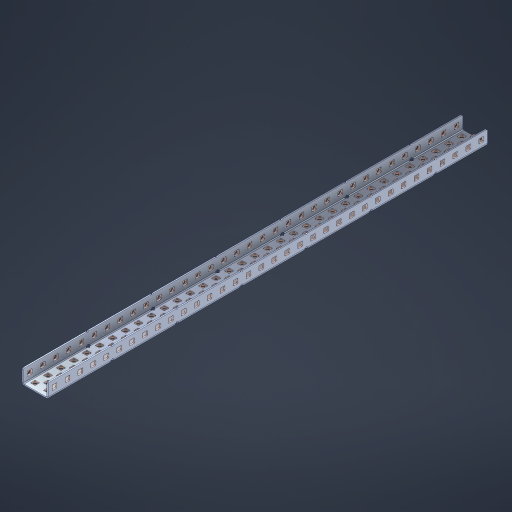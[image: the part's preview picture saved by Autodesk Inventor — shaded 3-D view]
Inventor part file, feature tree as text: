
AUTODESK INVENTOR PART (.ipt)
format: ipt  version: 2023 (Build 270158000, 158)  size: 2,078,720 bytes
history: native  units: in
note: dims shown in document units (in); Inventor stores cm internally (conversion verified against a paired STEP export)
features: other x177, extrude x168, sheet_metal_op x11, sketch x10, pattern_linear x2, mirror x1, chamfer x1
ambient origin geometry x8: Origin, YZ Plane, XZ Plane, XY Plane, X Axis, Y Axis, Z Axis, Center Point
bodies: Solid1 (feature_tree), Body (feature_tree)
feature tree (370):
  sheet_metal_op  "Flanges"
  other  "Flange Pattern Plane"
  other  "Flange Pattern Sketch"
  sheet_metal_op  "Flange Pattern"
  sheet_metal_op  "Body Pattern"
  pattern_linear  "Center Pattern"  Spacing1=0.0469in  [1 undecoded]
  other  "Arc Length"
  mirror  "Notch Mirror"
  pattern_linear  "Notch Pattern"  Spacing1=0.182in  [1 undecoded]
  chamfer  "End Chamfer"
  extrude  "Half Cut"  Depth=0.02in
  sketch  "Sketch1"  dims[d0=1.0in]
  other  "Plate1"
  sketch  "Sketch2"  dims[d1=17.0in]
  other  "Plate2"
  sheet_metal_op  "Bend1"
  sheet_metal_op  "Corner1"
  sketch  "Sketch3"  dims[d2=0.0469in]
  sketch  "Sketch7"  dims[d3=0.0469in]
  other  "Srf1"
  other  "Srf2"
  sketch  "Sketch8"  dims[d4=0.0234in]
  sketch  "Sketch9"  dims[d5=0.0938in]
  other  "Srf91"
  sheet_metal_op  "Body Pattern Sketch"
  other  "Srf92"
  sketch  "Sketch13"  dims[d6=0.0469in]
  sketch  "Sketch14"  dims[d7=0.5in d8=90.0deg d9=0.0312in]
  sketch  "Sketch15"  dims[d10=0.1875in]
  sketch  "Sketch16"  dims[d11=0.0469in d12=0.0469in d16=0.182in d17=0.02in d18=0.0469in d19=0.0in d20=0.25in d21=0.25in d38=13.3858in d40=0.5in d41=0.7874in d43=1.0in d46=0.172in d47=1.0in d48=0.0in d49=0.182in d50=0.02in d51=0.25in d52=0.25in d53=0.0469in d54=0.0in d55=0.172in d56=1.0in d57=0.0in d58=0.25in d60=13.3858in d62=0.5in d63=0.7874in d65=0.5in d85=0.1227in d86=0.1659in d88=0.04in d89=0.0469in d90=0.0in d91=0.04in d92=0.0491in d95=2.5in d96=0.04in d97=0.25in d98=45.0deg d99=0.25in d100=0.5in d101=0.0in d102=2.497in d106=0.182in d107=0.02in d108=0.5in d109=0.5in d110=0.0469in d111=0.0in d112=0.172in d113=0.5in d114=0.0in d117=0.5in d118=0.5in d119=0.5in]
  other  "Srf786"
  other  "Srf823"
  other  "Srf824"
  other  "Srf825"
  other  "Srf826"
  other  "Srf827"
  other  "Srf828"
  other  "Srf829"
  other  "Srf856"
  other  "Srf857"
  other  "Srf858"
  other  "Srf859"
  other  "Srf860"
  other  "Srf861"
  other  "Srf862"
  other  "Srf889"
  other  "Srf890"
  other  "Srf891"
  other  "Srf892"
  other  "Srf893"
  other  "Srf894"
  other  "Srf895"
  other  "Srf896"
  other  "Srf922"
  other  "Srf923"
  other  "Srf924"
  other  "Srf925"
  other  "Srf926"
  other  "Srf959"
  other  "Srf960"
  other  "Srf961"
  other  "Srf962"
  other  "Srf963"
  other  "Srf996"
  other  "Srf997"
  other  "Srf998"
  other  "Srf999"
  other  "Srf1000"
  other  "Srf1143"
  other  "Srf1144"
  other  "Srf1145"
  other  "Srf1146"
  other  "Srf1147"
  other  "Srf1148"
  other  "Srf1149"
  other  "Srf1150"
  other  "Srf1151"
  other  "Srf1152"
  other  "Srf1153"
  other  "Srf1154"
  other  "Srf1155"
  other  "Srf1156"
  other  "Srf1157"
  other  "Srf1158"
  other  "Srf1159"
  other  "Srf1160"
  other  "Srf1161"
  other  "Srf1162"
  other  "Srf1163"
  other  "Srf1164"
  other  "Srf1165"
  other  "Srf1166"
  other  "Srf1167"
  other  "Srf1168"
  other  "Srf1169"
  other  "Srf1170"
  other  "Srf1171"
  other  "Srf1172"
  other  "Srf1173"
  other  "Srf1174"
  other  "Srf1175"
  other  "Srf1176"
  other  "Srf1177"
  other  "Srf1178"
  other  "Srf1179"
  other  "Srf1180"
  other  "Srf1181"
  other  "Srf1182"
  other  "Srf1183"
  other  "Srf1184"
  other  "Srf1185"
  other  "Srf1186"
  other  "Srf1187"
  other  "Srf1188"
  other  "Srf1189"
  other  "Srf1190"
  other  "Srf1191"
  other  "Srf1192"
  other  "Srf1193"
  other  "Srf1194"
  other  "Srf1195"
  other  "Srf1196"
  other  "Srf1199"
  other  "Srf1200"
  other  "Srf1201"
  other  "Srf1202"
  other  "Srf1203"
  other  "Srf1204"
  other  "Srf1205"
  other  "Srf1206"
  other  "Srf1207"
  other  "Srf1208"
  other  "Srf1209"
  other  "Srf1210"
  other  "Srf1211"
  other  "Srf1212"
  other  "Srf1213"
  other  "Srf1214"
  other  "Srf1215"
  other  "Srf1216"
  other  "Srf1217"
  other  "Srf1218"
  other  "Srf1219"
  other  "Srf1220"
  other  "Srf1221"
  other  "Srf1222"
  other  "Srf1223"
  other  "Srf1224"
  other  "Srf1225"
  other  "Srf1226"
  other  "Srf1227"
  other  "Srf1228"
  other  "Srf1229"
  other  "Srf1230"
  other  "Srf1231"
  other  "Srf1232"
  other  "Srf1233"
  other  "Srf1234"
  other  "Srf1235"
  other  "Srf1236"
  other  "Srf1237"
  other  "Srf1238"
  other  "Srf1239"
  other  "Srf1240"
  other  "Srf1241"
  other  "Srf1242"
  other  "Srf1243"
  other  "Srf1244"
  other  "Srf1245"
  other  "Srf1246"
  other  "Srf1247"
  other  "Srf1248"
  other  "Srf1249"
  other  "Srf1250"
  other  "Srf1251"
  other  "Srf1252"
  other  "Srf1255"
  other  "Srf1256"
  other  "Srf1257"
  other  "Srf1258"
  other  "Srf1259"
  other  "Srf1260"
  other  "Srf1261"
  other  "Srf1262"
  other  "Srf1263"
  other  "Srf1264"
  other  "Srf1265"
  other  "Srf1266"
  other  "Srf1267"
  other  "Srf1268"
  other  "Srf1269"
  other  "Srf1270"
  other  "Srf1271"
  other  "Srf1272"
  other  "Srf1273"
  other  "Srf1274"
  sheet_metal_op  "Flange Stamp"
  sheet_metal_op  "Flange Circle"
  sheet_metal_op  "Body Stamp"
  sheet_metal_op  "Body Circle"
  other  "Center Stamp"
  other  "Center Circle"
  sheet_metal_op  "Notch"
  extrude  "ExtrusionSrf2"  Depth=0.0469in
  extrude  "ExtrusionSrf92"  TaperAngle=0.0deg  [1 undecoded]
  extrude  "ExtrusionSrf823"  Depth=0.5in
  extrude  "ExtrusionSrf824"  Depth=0.5in
  extrude  "ExtrusionSrf825"  Depth=0.5in
  extrude  "ExtrusionSrf826"  Depth=0.5in
  extrude  "ExtrusionSrf827"  Depth=1.0in TaperAngle=0.0deg
  extrude  "ExtrusionSrf828"  Depth=0.5in
  extrude  "ExtrusionSrf829"  Depth=0.02in
  extrude  "ExtrusionSrf856"  Depth=0.5in
  extrude  "ExtrusionSrf857"  Depth=0.5in
  extrude  "ExtrusionSrf858"  Depth=0.0469in
  extrude  "ExtrusionSrf859"  TaperAngle=0.0deg  [1 undecoded]
  extrude  "ExtrusionSrf860"  Depth=0.5in
  extrude  "ExtrusionSrf861"  Depth=1.0in TaperAngle=0.0deg
  extrude  "ExtrusionSrf862"  Depth=0.5in
  extrude  "ExtrusionSrf889"  Depth=0.5in
  extrude  "ExtrusionSrf890"  Depth=0.5in
  extrude  "ExtrusionSrf891"  Depth=0.5in
  extrude  "ExtrusionSrf892"  Depth=0.5in
  extrude  "ExtrusionSrf893"  Depth=0.5in
  extrude  "ExtrusionSrf894"  Depth=0.0469in
  extrude  "ExtrusionSrf895"  TaperAngle=0.0deg  [1 undecoded]
  extrude  "ExtrusionSrf896"  Depth=0.5in
  extrude  "ExtrusionSrf922"  Depth=0.5in
  extrude  "ExtrusionSrf923"  Depth=2.5in
  extrude  "ExtrusionSrf924"  Depth=0.5in TaperAngle=45.0deg
  extrude  "ExtrusionSrf925"  Depth=0.5in
  extrude  "ExtrusionSrf926"  Depth=0.5in TaperAngle=0.0deg
  extrude  "ExtrusionSrf959"  Depth=0.5in
  extrude  "ExtrusionSrf960"  Depth=0.5in
  extrude  "ExtrusionSrf961"  Depth=0.02in
  extrude  "ExtrusionSrf962"  Depth=0.5in
  extrude  "ExtrusionSrf963"  Depth=0.5in
  extrude  "ExtrusionSrf996"  Depth=0.0469in
  extrude  "ExtrusionSrf997"  TaperAngle=0.0deg  [1 undecoded]
  extrude  "ExtrusionSrf998"  Depth=0.5in
  extrude  "ExtrusionSrf999"  Depth=0.5in TaperAngle=0.0deg
  extrude  "ExtrusionSrf1000"  Depth=0.5in
  extrude  "ExtrusionSrf1143"  Depth=0.5in
  extrude  "ExtrusionSrf1144"  Depth=0.5in
  extrude  "ExtrusionSrf1145"  [1 undecoded]
  extrude  "ExtrusionSrf1146"  [1 undecoded]
  extrude  "ExtrusionSrf1147"  [1 undecoded]
  extrude  "ExtrusionSrf1148"  [1 undecoded]
  extrude  "ExtrusionSrf1149"  [1 undecoded]
  extrude  "ExtrusionSrf1150"  [1 undecoded]
  extrude  "ExtrusionSrf1151"  [1 undecoded]
  extrude  "ExtrusionSrf1152"  [1 undecoded]
  extrude  "ExtrusionSrf1153"  [1 undecoded]
  extrude  "ExtrusionSrf1154"  [1 undecoded]
  extrude  "ExtrusionSrf1155"  [1 undecoded]
  extrude  "ExtrusionSrf1156"  [1 undecoded]
  extrude  "ExtrusionSrf1157"  [1 undecoded]
  extrude  "ExtrusionSrf1158"  [1 undecoded]
  extrude  "ExtrusionSrf1159"  [1 undecoded]
  extrude  "ExtrusionSrf1160"  [1 undecoded]
  extrude  "ExtrusionSrf1161"  [1 undecoded]
  extrude  "ExtrusionSrf1162"  [1 undecoded]
  extrude  "ExtrusionSrf1163"  [1 undecoded]
  extrude  "ExtrusionSrf1164"  [1 undecoded]
  extrude  "ExtrusionSrf1165"  [1 undecoded]
  extrude  "ExtrusionSrf1166"  [1 undecoded]
  extrude  "ExtrusionSrf1167"  [1 undecoded]
  extrude  "ExtrusionSrf1168"  [1 undecoded]
  extrude  "ExtrusionSrf1169"  [1 undecoded]
  extrude  "ExtrusionSrf1170"  [1 undecoded]
  extrude  "ExtrusionSrf1171"  [1 undecoded]
  extrude  "ExtrusionSrf1172"  [1 undecoded]
  extrude  "ExtrusionSrf1173"  [1 undecoded]
  extrude  "ExtrusionSrf1174"  [1 undecoded]
  extrude  "ExtrusionSrf1175"  [1 undecoded]
  extrude  "ExtrusionSrf1176"  [1 undecoded]
  extrude  "ExtrusionSrf1177"  [1 undecoded]
  extrude  "ExtrusionSrf1178"  [1 undecoded]
  extrude  "ExtrusionSrf1179"  [1 undecoded]
  extrude  "ExtrusionSrf1180"  [1 undecoded]
  extrude  "ExtrusionSrf1181"  [1 undecoded]
  extrude  "ExtrusionSrf1182"  [1 undecoded]
  extrude  "ExtrusionSrf1183"  [1 undecoded]
  extrude  "ExtrusionSrf1184"  [1 undecoded]
  extrude  "ExtrusionSrf1185"  [1 undecoded]
  extrude  "ExtrusionSrf1186"  [1 undecoded]
  extrude  "ExtrusionSrf1187"  [1 undecoded]
  extrude  "ExtrusionSrf1188"  [1 undecoded]
  extrude  "ExtrusionSrf1189"  [1 undecoded]
  extrude  "ExtrusionSrf1190"  [1 undecoded]
  extrude  "ExtrusionSrf1191"  [1 undecoded]
  extrude  "ExtrusionSrf1192"  [1 undecoded]
  extrude  "ExtrusionSrf1193"  [1 undecoded]
  extrude  "ExtrusionSrf1194"  [1 undecoded]
  extrude  "ExtrusionSrf1195"  [1 undecoded]
  extrude  "ExtrusionSrf1196"  [1 undecoded]
  extrude  "ExtrusionSrf1199"  [1 undecoded]
  extrude  "ExtrusionSrf1200"  [1 undecoded]
  extrude  "ExtrusionSrf1201"  [1 undecoded]
  extrude  "ExtrusionSrf1202"  [1 undecoded]
  extrude  "ExtrusionSrf1203"  [1 undecoded]
  extrude  "ExtrusionSrf1204"  [1 undecoded]
  extrude  "ExtrusionSrf1205"  [1 undecoded]
  extrude  "ExtrusionSrf1206"  [1 undecoded]
  extrude  "ExtrusionSrf1207"  [1 undecoded]
  extrude  "ExtrusionSrf1208"  [1 undecoded]
  extrude  "ExtrusionSrf1209"  [1 undecoded]
  extrude  "ExtrusionSrf1210"  [1 undecoded]
  extrude  "ExtrusionSrf1211"  [1 undecoded]
  extrude  "ExtrusionSrf1212"  [1 undecoded]
  extrude  "ExtrusionSrf1213"  [1 undecoded]
  extrude  "ExtrusionSrf1214"  [1 undecoded]
  extrude  "ExtrusionSrf1215"  [1 undecoded]
  extrude  "ExtrusionSrf1216"  [1 undecoded]
  extrude  "ExtrusionSrf1217"  [1 undecoded]
  extrude  "ExtrusionSrf1218"  [1 undecoded]
  extrude  "ExtrusionSrf1219"  [1 undecoded]
  extrude  "ExtrusionSrf1220"  [1 undecoded]
  extrude  "ExtrusionSrf1221"  [1 undecoded]
  extrude  "ExtrusionSrf1222"  [1 undecoded]
  extrude  "ExtrusionSrf1223"  [1 undecoded]
  extrude  "ExtrusionSrf1224"  [1 undecoded]
  extrude  "ExtrusionSrf1225"  [1 undecoded]
  extrude  "ExtrusionSrf1226"  [1 undecoded]
  extrude  "ExtrusionSrf1227"  [1 undecoded]
  extrude  "ExtrusionSrf1228"  [1 undecoded]
  extrude  "ExtrusionSrf1229"  [1 undecoded]
  extrude  "ExtrusionSrf1230"  [1 undecoded]
  extrude  "ExtrusionSrf1231"  [1 undecoded]
  extrude  "ExtrusionSrf1232"  [1 undecoded]
  extrude  "ExtrusionSrf1233"  [1 undecoded]
  extrude  "ExtrusionSrf1234"  [1 undecoded]
  extrude  "ExtrusionSrf1235"  [1 undecoded]
  extrude  "ExtrusionSrf1236"  [1 undecoded]
  extrude  "ExtrusionSrf1237"  [1 undecoded]
  extrude  "ExtrusionSrf1238"  [1 undecoded]
  extrude  "ExtrusionSrf1239"  [1 undecoded]
  extrude  "ExtrusionSrf1240"  [1 undecoded]
  extrude  "ExtrusionSrf1241"  [1 undecoded]
  extrude  "ExtrusionSrf1242"  [1 undecoded]
  extrude  "ExtrusionSrf1243"  [1 undecoded]
  extrude  "ExtrusionSrf1244"  [1 undecoded]
  extrude  "ExtrusionSrf1245"  [1 undecoded]
  extrude  "ExtrusionSrf1246"  [1 undecoded]
  extrude  "ExtrusionSrf1247"  [1 undecoded]
  extrude  "ExtrusionSrf1248"  [1 undecoded]
  extrude  "ExtrusionSrf1249"  [1 undecoded]
  extrude  "ExtrusionSrf1250"  [1 undecoded]
  extrude  "ExtrusionSrf1251"  [1 undecoded]
  extrude  "ExtrusionSrf1252"  [1 undecoded]
  extrude  "ExtrusionSrf1255"  [1 undecoded]
  extrude  "ExtrusionSrf1256"  [1 undecoded]
  extrude  "ExtrusionSrf1257"  [1 undecoded]
  extrude  "ExtrusionSrf1258"  [1 undecoded]
  extrude  "ExtrusionSrf1259"  [1 undecoded]
  extrude  "ExtrusionSrf1260"  [1 undecoded]
  extrude  "ExtrusionSrf1261"  [1 undecoded]
  extrude  "ExtrusionSrf1262"  [1 undecoded]
  extrude  "ExtrusionSrf1263"  [1 undecoded]
  extrude  "ExtrusionSrf1264"  [1 undecoded]
  extrude  "ExtrusionSrf1265"  [1 undecoded]
  extrude  "ExtrusionSrf1266"  [1 undecoded]
  extrude  "ExtrusionSrf1267"  [1 undecoded]
  extrude  "ExtrusionSrf1268"  [1 undecoded]
  extrude  "ExtrusionSrf1269"  [1 undecoded]
  extrude  "ExtrusionSrf1270"  [1 undecoded]
  extrude  "ExtrusionSrf1271"  [1 undecoded]
  extrude  "ExtrusionSrf1272"  [1 undecoded]
  extrude  "ExtrusionSrf1273"  [1 undecoded]
  extrude  "ExtrusionSrf1274"  [1 undecoded]
note: 132 required parameter values undecoded (feature->parameter linkage not recoverable at this tier; creation-order binding heuristic only, values carry confidence <= 0.55)
